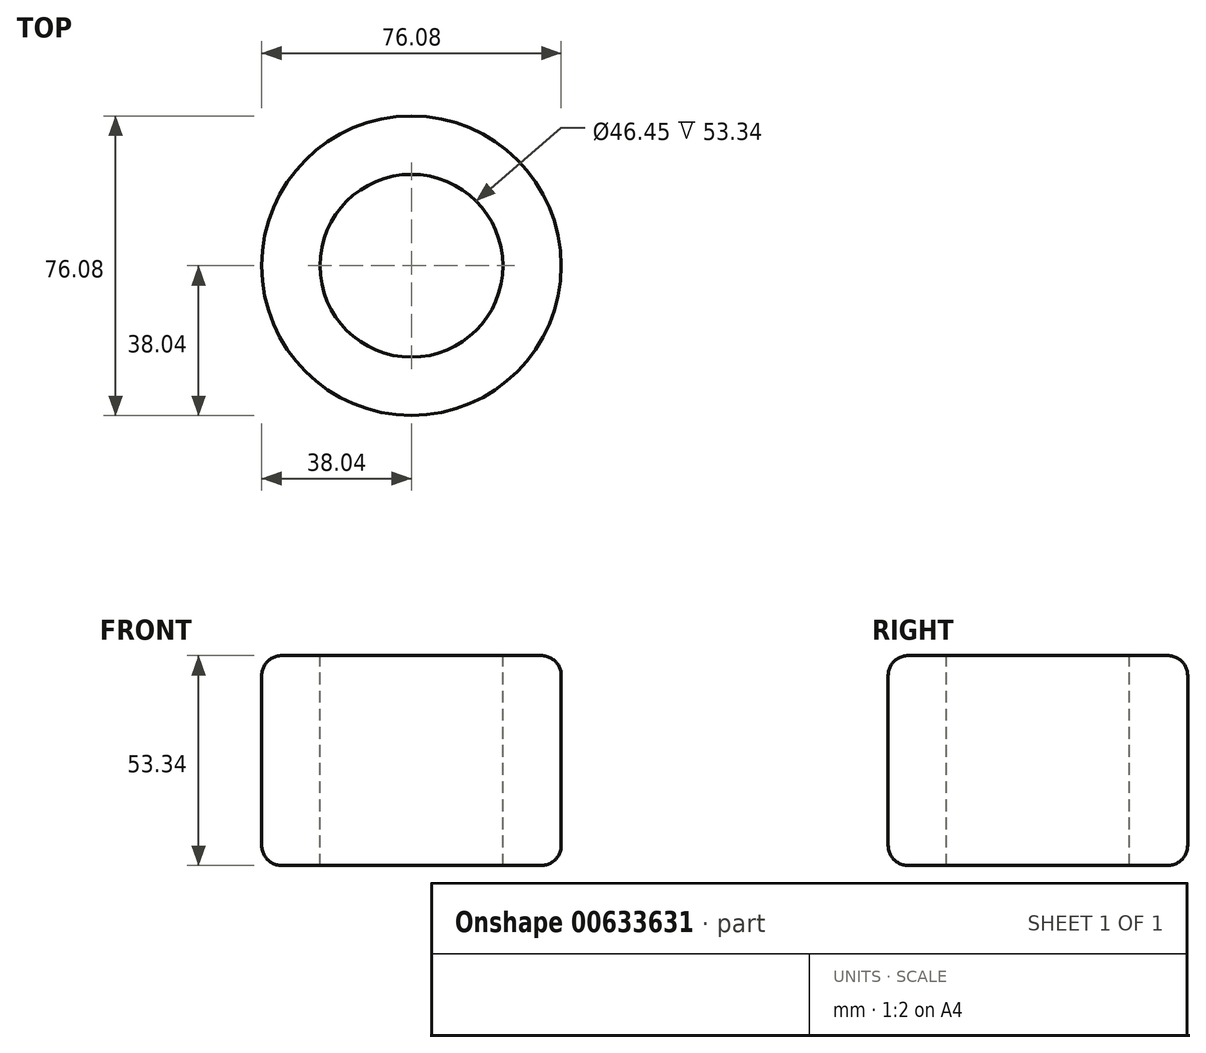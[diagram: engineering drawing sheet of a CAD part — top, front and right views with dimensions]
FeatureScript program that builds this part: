
annotation { "Feature Type Name" : "Feature", "Feature Type Description" : "" }
export const myFeature = defineFeature(function(context is Context, id is Id, definition is map)
    precondition{}
    {
        {
            var Q0;
            Q0=qCreatedBy(makeId("Top.planeOp"),FACE);
            var sketch = newSketch(context, id + "F0", { "sketchPlane" : qUnion([Q0])});
            skCircle(sketch, "E0", {"center": v(0, 0) * mm, "radius": 38.04 * mm});
            skSolve(sketch);
        }
        {
            var Q0;
            Q0 = qSketchRegion(id + "F0", true);
            extrude(context, id + "F1", {"entities" : qUnion([Q0]), "depth" : 53.34 * mm, "offsetDistance" : 25.4 * mm});
        }
        {
            var Q0;
            Q0=makeQuery(id+"F1.opExtrude","CAP_FACE",FACE,{"disambiguationData":[OSD([sQuery(id+"F0.wireOp",EDGE,"E0")])],"isStart":false});
            var sketch = newSketch(context, id + "F2", { "sketchPlane" : qUnion([Q0])});
            skCircle(sketch, "E1", {"center": v(0, 0) * mm, "radius": 23.22 * mm});
            skSolve(sketch);
        }
        {
            var Q0;
            Q0=makeQuery(id+"F2.imprint","IMPRINT",FACE,{"disambiguationData":[TD([[makeQuery(id+"F2.imprint","IMPRINT",EDGE,{"derivedFrom":sQuery(id+"F2.wireOp",EDGE,"E1")}),1.0]])]});
            extrude(context, id + "F3", {"entities" : qUnion([Q0]), "operationType" : NewBodyOperationType.REMOVE, "flatOperationType" : FlatOperationType.REMOVE, "endBound" : BoundingType.UP_TO_NEXT, "oppositeDirection" : true, "depth" : 91.19 * mm, "offsetDistance" : 25.4 * mm, "domain" : OperationDomain.MODEL});
        }
        {
            var Q0;
            Q0=makeQuery(id+"F1.opExtrude","CAP_EDGE",EDGE,{"disambiguationData":[OSD([sQuery(id+"F0.wireOp",EDGE,"E0")])],"isStart":false});
            var Q1;
            Q1=makeQuery(id+"F3.boolean.opBoolean","COPY",EDGE,{"derivedFrom":makeQuery(id+"F3.opExtrude","CAP_EDGE",EDGE,{"disambiguationData":[OSD([sQuery(id+"F2.wireOp",EDGE,"E1")])],"isStart":true})});
            var Q2;
            Q2=makeQuery(id+"F1.opExtrude","CAP_EDGE",EDGE,{"disambiguationData":[OSD([sQuery(id+"F0.wireOp",EDGE,"E0")])],"isStart":true});
            var Q3;
            Q3=makeQuery(id+"F3.boolean.opBoolean","COPY",EDGE,{"derivedFrom":makeQuery(id+"F3.opExtrude","CAP_EDGE",EDGE,{"disambiguationData":[OSD([sQuery(id+"F2.wireOp",EDGE,"E1")])],"isStart":false})});
            fillet(context, id + "F4", {"entities" : qUnion([Q0, Q1, Q2, Q3]), "radius" : 5.08 * mm, "tangentPropagation" : true, "allowEdgeOverflow" : false});
        }
    });
